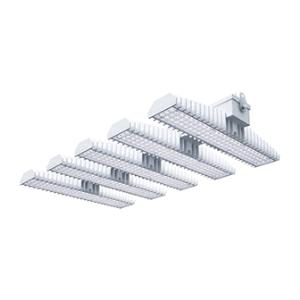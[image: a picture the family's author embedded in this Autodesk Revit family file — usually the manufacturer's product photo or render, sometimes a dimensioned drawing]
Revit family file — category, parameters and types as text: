
# Revit family: 3f_filippi_-_3f_lem_ampio_3f_filippi_-_58886_a0811_-_3f_lem_5_led_250_cr_ampio___vt_8662
name_source: partatom
category: Lighting Fixtures
units: mm (PartAtom-declared; Revit-internal decimal feet)

## family parameters
Cut with Voids When Loaded = No
Host = Face
Light Source = No
Part Type = Normal
Room Calculation Point = No
Round Connector Dimension = Use Diameter
Shared = No

## types (1)
- 3F Filippi - 3F LEM Ampio (1 x LED, 39552 lm, 274 W, 4000 K)
    Apparent Load = 274 VA
    Approval mark = CE
    CIE Flux Codes = 60 92 99 100 100
    Color Rendering = 80
    Color Temperature = 4000 K
    Control Gear = Electronic ballast
    Default Elevation = 1800 mm
    Description = Industrial luminaire with high light output and high luminous efficiency designed with the most innovative technologies for environments with temperature up to 55°C.

ILLUMINOTECHNICAL
Luminous efficiency 100% (DLOR 99%, ULOR 1%).
Initial luminous flux of the luminaire 39552 lm.
Direct symmetric wide distribution: the illuminated area has a rectangular shape.
Installation Interdistance Transv.D = 1.58 x hu - Long.D = 1.45 x hu.
Tabular UGR (CIE 117 - 4H-8H; S=0.25H; 70/50/20): RUG 22.9 - 23.9.
Beam angle: 93° - 99°.
Luminous efficacy 144 lm/W.
Lifetime (L93/B10): 30000 h. (tq+25°C)
Lifetime (L90/B10): 50000 h. (tq+25°C)
Lifetime (L85/B10): 80000 h. (tq+25°C)
Lifetime (L80/B10): 100000 h. (tq+25°C)
Lifetime (L85/B10): 50000 h. (tq+55°C)
Sudden decreased luminous flux after 50000 hours: 0% (C0).
Photobiological safety in compliance with IEC/TR 62778: RG0 risk exempt, (IEC 62471).
In compliance with IEC/EN 62722-2-1 - IEC/EN 62717 standards.

SOURCE
5 Mid-Power linear LED modules 50W/840.
Energy efficiency class (UE 2019/2020 - UE 2019/2015): C.
CIE 13.3 Colour rendering index: CRI >80 (R9 <50%).
IES TM-30 Fidelity Index: Rf = 84 Rg = 95.
CCT nominal colour temperature 4000 K.
Colour initial tolerance (MacAdam): SDCM 3.

MECHANICAL
Passive modular heatsinks in die-casted aluminium, painted in white colour.
To optimize the thermal management of the LED module, the heatsinks are oversized and provided with self-cleaning of cooling fins.
Wiring body in aluminium and galvanised steel anchored solidly to the sinks and thermally separated.
3F Lens lenses with high luminous efficiency, transparent methacrylate (PMMA), fixed to the LED modules.
Fixing brackets in stainless steel.
Luminaire with limited surface temperature. - D - (EN 60598-2-24)
Dimensions: 952x542 mm, height 133 mm. Weight 23.385 kg.
IP65 protection degree.
Mechanical strength to impacts IK06 (1 joule).
Glow-wire test resistance 650°C.

ELECTRICAL
Halogen Free electronic wiring 230V-50/60Hz, power factor 0.97, THD <25%, constant output current, class I, 3 driver.
Power of the luminaire 274 W.
ENEC - CE.
SAFE FLICKER: PstLM=<1 and SVM=<0.4 (IEC TR 61547-1 and IEC TR 63158), to ensure a more comfortable and safe light.
Luminaire compliant with EN 60598-2-22 for power supply from a centralised emergency system CPSS (Central Power Supply System), not incorporated in the luminaire - high risk areas excluded. The default power and flux are 100% in AC and 100% in DC.
Ambient temperature from -30°C to +55°C.
Temperature class T6 max 85°C.
Quick connection via M20 3P connector with 9-13 mm tightening range.
Power unit positioned on a separate compartment by the LED module to ensure optimum temperatures of cabling components, to be inspectable and maintainable.
Relative humidity UR: <85%.

INSTALLATION
Ceiling / Suspended / Wall.
All accessories dedicated to this product are available on the Catalog and on our website www.3F-Filippi.com.

ACCESSORIES
A0811 - VT transparent glass, tempered, not flammable, with sealing gasket.
One required for each light module. The pack contains 10 pieces.

APPLICATIONS
In commercial environments, exhibition and industrial areas, stores, open areas.
Applications with high ambient temperature up to 55°C.
Environments in which it is necessary a total protection against falling fragments (eg environments with foodstuffs or machines with moving parts or with extreme temperature changes), use luminaires with polycarbonate lenses.

WARNING
Fixture not suitable for cold stores with an ambient temperature <0°C and/or relative humidity >85%.
Luminaire designed for disposal/recycling at end-of-life.
Replaceable (LED only) light source by a professional. Replaceable control gear by a professional.
    Height = 133 mm  [stored 0.436352 ft]
    Lamp = 1 x LED
    Lamp Light Flux = 39552 lm
    Lamp Power = 274 W
    Lamp count = 1
    Length = 952 mm
    Lifetime = 50000 h
    Luminous efficacy = 144 lm/W
    Manufacturer = 3F Filippi
    ModVariant = No
    Model = 3F Filippi - 58886+A0811 - 3F LEM 5 LED 250 CR AMPIO + VT
    Mounting Place = Ceiling
    Mounting Type = Pendant
    Number of Poles = 1
    OnlyDefault = Yes
    Power Factor = 1
    Product Name = 3F Filippi - 3F LEM Ampio
    Product group = pendant luminaire
    ProductGroupID = 9
    Protection Class = Protection class I
    Protection Degree = IP 65
    RLX_Detail_Level = 1
    RLX_Emergency_Light_Flux = 0 lm
    RLX_Emergency_Type = 0
    RLX_Emergency_Type_DB = No
    RlxData = <blob elided: 126709 chars, md5=dc50e73e>
    Socket = socket
    Standby Power = 0 W
    System Light Flux = 39552 lm
    System Power = 274 W
    Type Comments = Product without accessories
    Type Image = 3f_filippi_-_lem_5__a0811.jpg
    URL = http://relux.com
    VarID = ---
    Voltage = 0 V
    Weight = 0.00 kg
    Width = 542 mm

note: [stored X ft] marks values corroborated as IEEE doubles in the binary element streams (Revit-internal decimal feet)

## geometry (parser evidence)
native form markers: Blend x4, Sweep x12
no freeform markers — native parametric forms only
